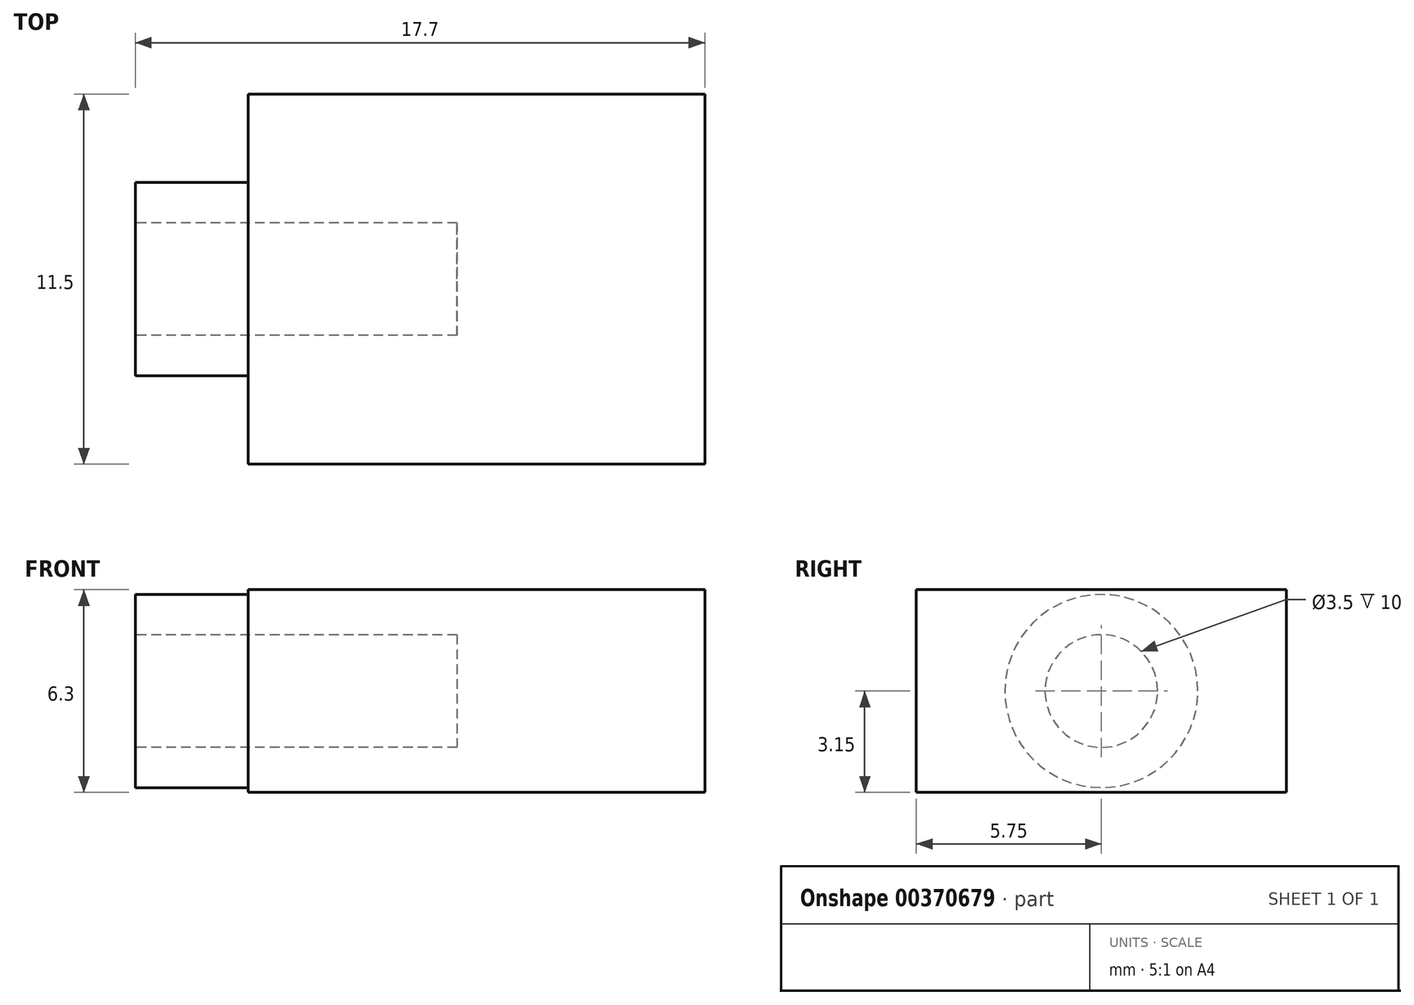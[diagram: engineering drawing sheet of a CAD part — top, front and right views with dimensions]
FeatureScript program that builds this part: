
annotation { "Feature Type Name" : "Feature", "Feature Type Description" : "" }
export const myFeature = defineFeature(function(context is Context, id is Id, definition is map)
    precondition{}
    {
        {
            var Q0;
            Q0=qCreatedBy(makeId("Front.planeOp"),FACE);
            var sketch = newSketch(context, id + "F0", { "sketchPlane" : qUnion([Q0])});
            skLineSegment(sketch, "E0.bottom", {"start": v(0, 0) * mm, "end": v(14.2, 0) * mm});
            skLineSegment(sketch, "E0.top", {"start": v(0, 6.3) * mm, "end": v(14.2, 6.3) * mm});
            skLineSegment(sketch, "E0.left", {"start": v(0, 0) * mm, "end": v(0, 6.3) * mm});
            skLineSegment(sketch, "E0.right", {"start": v(14.2, 0) * mm, "end": v(14.2, 6.3) * mm});
            skSolve(sketch);
        }
        {
            var Q0;
            Q0 = qSketchRegion(id + "F0", true);
            extrude(context, id + "F1", {"entities" : qUnion([Q0]), "depth" : 11.5 * mm});
        }
        {
            var Q0;
            Q0=makeQuery(id+"F1.opExtrude","SWEPT_FACE",FACE,{"disambiguationData":[OSD([sQuery(id+"F0.wireOp",EDGE,"E0.left")])]});
            var sketch = newSketch(context, id + "F2", { "sketchPlane" : qUnion([Q0])});
            skCircle(sketch, "E1", {"center": v(5.75, 3.15) * mm, "radius": 3 * mm});
            skPoint(sketch, "E1.centerSnap0", {"position": v(0, 3.15) * mm});
            skPoint(sketch, "E1.centerSnap1", {"position": v(5.75, 6.3) * mm});
            skSolve(sketch);
        }
        {
            var Q0;
            Q0 = qSketchRegion(id + "F2", true);
            extrude(context, id + "F3", {"entities" : qUnion([Q0]), "operationType" : NewBodyOperationType.ADD, "depth" : 3.5 * mm});
        }
        {
            var Q0;
            Q0=makeQuery(id+"F3.opExtrude","CAP_FACE",FACE,{"disambiguationData":[OSD([sQuery(id+"F2.wireOp",EDGE,"E1")])],"isStart":false});
            var sketch = newSketch(context, id + "F4", { "sketchPlane" : qUnion([Q0])});
            skCircle(sketch, "E2", {"center": v(5.75, 3.15) * mm, "radius": 1.75 * mm});
            skSolve(sketch);
        }
        {
            var Q0;
            Q0 = qSketchRegion(id + "F4", true);
            extrude(context, id + "F5", {"entities" : qUnion([Q0]), "operationType" : NewBodyOperationType.REMOVE, "oppositeDirection" : true, "depth" : 10 * mm});
        }
    });
